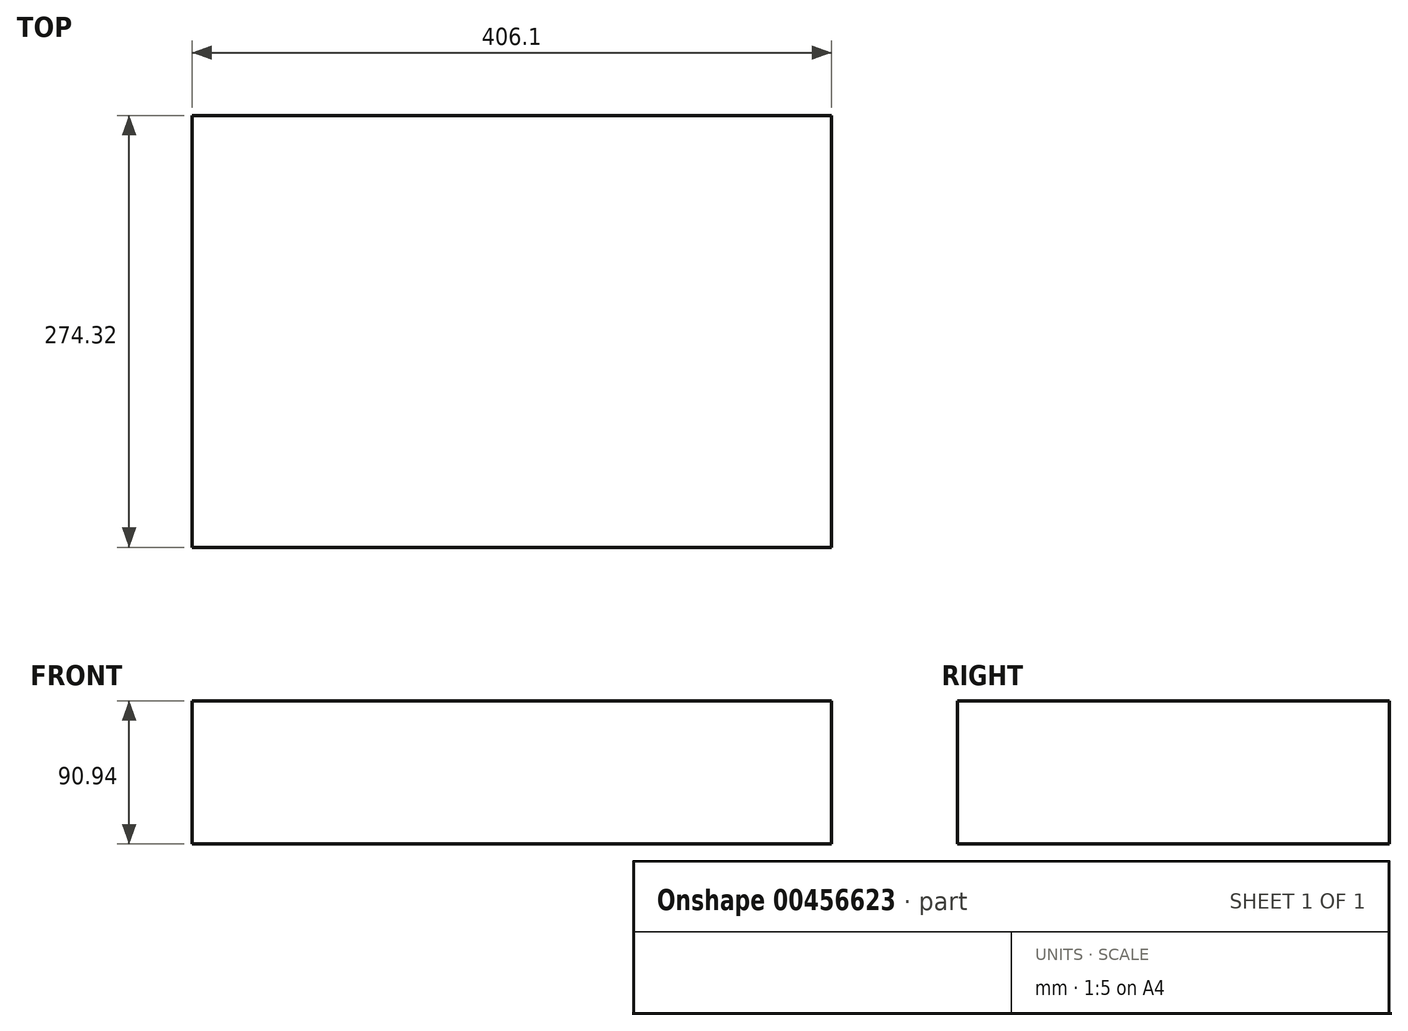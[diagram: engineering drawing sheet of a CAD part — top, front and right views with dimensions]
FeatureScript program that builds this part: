
annotation { "Feature Type Name" : "Feature", "Feature Type Description" : "" }
export const myFeature = defineFeature(function(context is Context, id is Id, definition is map)
    precondition{}
    {
        {
            var Q0;
            Q0=qCreatedBy(makeId("Front.planeOp"),FACE);
            var sketch = newSketch(context, id + "F0", { "sketchPlane" : qUnion([Q0])});
            skLineSegment(sketch, "E0.bottom", {"start": v(-50.65, 45.47) * mm, "end": v(50.65, 45.47) * mm});
            skLineSegment(sketch, "E0.top", {"start": v(-50.65, -45.47) * mm, "end": v(50.65, -45.47) * mm});
            skLineSegment(sketch, "E0.left", {"start": v(-50.65, 45.47) * mm, "end": v(-50.65, -45.47) * mm});
            skLineSegment(sketch, "E0.right", {"start": v(50.65, 45.47) * mm, "end": v(50.65, -45.47) * mm});
            skPoint(sketch, "E0.middle", {"position": v(0, 0) * mm});
            skSolve(sketch);
        }
        {
            var Q0;
            Q0=makeQuery(id+"F0.imprint","IMPRINT",FACE,{"disambiguationData":[TD([[makeQuery(id+"F0.imprint","IMPRINT",EDGE,{"derivedFrom":sQuery(id+"F0.wireOp",EDGE,"E0.bottom")}),-1.0]])]});
            extrude(context, id + "F1", {"entities" : qUnion([Q0]), "depth" : 274.32 * mm});
        }
        {
            var Q0;
            Q0=makeQuery(id+"F1.opExtrude","SWEPT_FACE",FACE,{"disambiguationData":[OSD([sQuery(id+"F0.wireOp",EDGE,"E0.left")])]});
            extrude(context, id + "F2", {"entities" : qUnion([Q0]), "operationType" : NewBodyOperationType.ADD, "depth" : 304.8 * mm});
        }
    });
